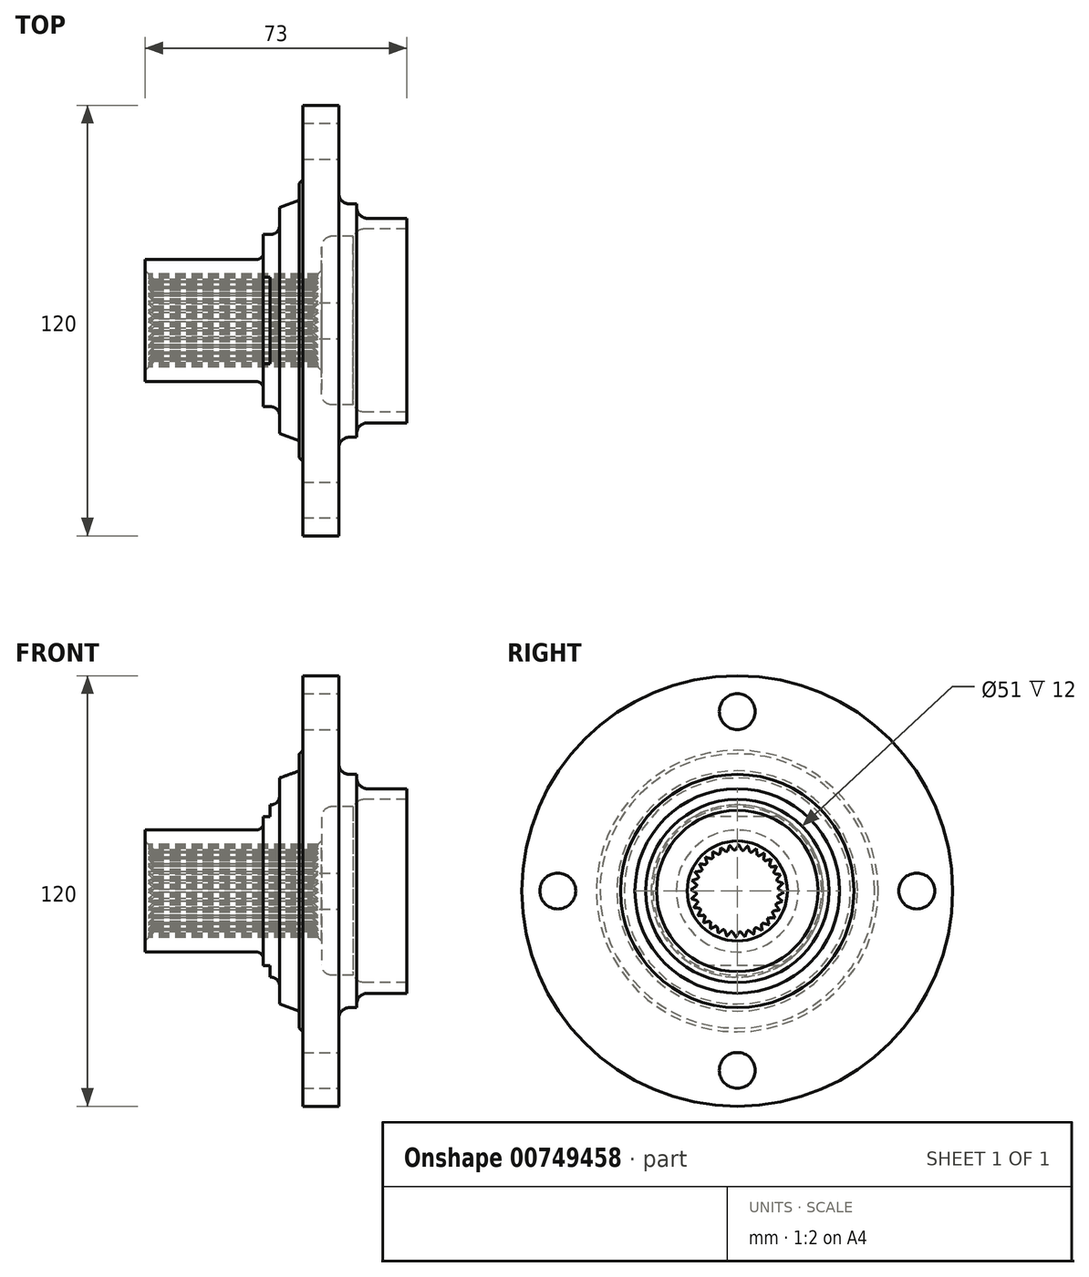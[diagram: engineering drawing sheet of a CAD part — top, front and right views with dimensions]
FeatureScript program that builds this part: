
annotation { "Feature Type Name" : "Feature", "Feature Type Description" : "" }
export const myFeature = defineFeature(function(context is Context, id is Id, definition is map)
    precondition{}
    {
        {
            var Q0;
            Q0=qCreatedBy(makeId("Front.planeOp"),FACE);
            var sketch = newSketch(context, id + "F0", { "sketchPlane" : qUnion([Q0])});
            skLineSegment(sketch, "E0", {"start": v(0, 0) * mm, "end": v(66.1, 0) * mm, "construction": true});
            skLineSegment(sketch, "E1", {"start": v(0, 17) * mm, "end": v(31, 17) * mm});
            skLineSegment(sketch, "E2", {"start": v(33, 19) * mm, "end": v(33, 24) * mm});
            skLineSegment(sketch, "E3", {"start": v(33, 24) * mm, "end": v(35, 24) * mm});
            skLineSegment(sketch, "E4", {"start": v(37.5, 26.5) * mm, "end": v(37.5, 31.5) * mm});
            skLineSegment(sketch, "E5", {"start": v(43, 33.5) * mm, "end": v(43, 38.25) * mm});
            skLineSegment(sketch, "E6", {"start": v(44, 39.25) * mm, "end": v(44, 60) * mm});
            skLineSegment(sketch, "E7", {"start": v(44, 60) * mm, "end": v(54, 60) * mm});
            skLineSegment(sketch, "E8", {"start": v(54, 60) * mm, "end": v(54, 35.5) * mm});
            skLineSegment(sketch, "E9", {"start": v(37.5, 31.5) * mm, "end": v(43, 33.5) * mm});
            skLineSegment(sketch, "E10", {"start": v(43, 38.25) * mm, "end": v(44, 39.25) * mm});
            skLineSegment(sketch, "E11", {"start": v(57, 32.5) * mm, "end": v(59, 32.5) * mm});
            skLineSegment(sketch, "E12", {"start": v(59, 32.5) * mm, "end": v(59, 31.5) * mm});
            skLineSegment(sketch, "E13", {"start": v(62, 28.5) * mm, "end": v(73, 28.5) * mm});
            skLineSegment(sketch, "E14", {"start": v(73, 28.5) * mm, "end": v(73, 25.5) * mm});
            skLineSegment(sketch, "E15", {"start": v(73, 25.5) * mm, "end": v(61, 25.5) * mm});
            skLineSegment(sketch, "E16", {"start": v(58, 23.5) * mm, "end": v(58, 22.5) * mm});
            skLineSegment(sketch, "E17", {"start": v(58, 23.5) * mm, "end": v(52.2, 23.5) * mm});
            skLineSegment(sketch, "E18", {"start": v(49.2, 20.5) * mm, "end": v(49.2, 11.45) * mm});
            skLineSegment(sketch, "E19", {"start": v(49.2, 11.45) * mm, "end": v(0, 11.45) * mm});
            skLineSegment(sketch, "E20", {"start": v(0, 11.45) * mm, "end": v(0, 17) * mm});
            skPoint(sketch, "E21.visualSharp", {"position": v(54, 32.5) * mm});
            skArc(sketch, "E21.filletArc", {"start": v(54, 35.5) * mm, "mid": v(54.88, 33.38) * mm, "end": v(57, 32.5) * mm});
            skPoint(sketch, "E22.visualSharp", {"position": v(59, 28.5) * mm});
            skArc(sketch, "E22.filletArc", {"start": v(59, 31.5) * mm, "mid": v(59.88, 29.38) * mm, "end": v(62, 28.5) * mm});
            skPoint(sketch, "E23.visualSharp", {"position": v(37.5, 24) * mm});
            skArc(sketch, "E23.filletArc", {"start": v(35, 24) * mm, "mid": v(36.77, 24.73) * mm, "end": v(37.5, 26.5) * mm});
            skPoint(sketch, "E24.visualSharp", {"position": v(33, 17) * mm});
            skArc(sketch, "E24.filletArc", {"start": v(31, 17) * mm, "mid": v(32.41, 17.59) * mm, "end": v(33, 19) * mm});
            skPoint(sketch, "E25.visualSharp", {"position": v(58, 25.5) * mm});
            skArc(sketch, "E25.filletArc", {"start": v(61, 25.5) * mm, "mid": v(58.88, 24.62) * mm, "end": v(58, 22.5) * mm});
            skPoint(sketch, "E26.visualSharp", {"position": v(49.2, 23.5) * mm});
            skArc(sketch, "E26.filletArc", {"start": v(52.2, 23.5) * mm, "mid": v(50.08, 22.62) * mm, "end": v(49.2, 20.5) * mm});
            skSolve(sketch);
        }
        {
            var Q0;
            Q0=makeQuery(id+"F0.imprint","IMPRINT",FACE,{"disambiguationData":[TD([[makeQuery(id+"F0.imprint","IMPRINT",EDGE,{"derivedFrom":sQuery(id+"F0.wireOp",EDGE,"E1")}),-1.0]])]});
            var Q1;
            Q1=sQuery(id+"F0.wireOp",EDGE,"E0");
            revolve(context, id + "F1", {"surfaceOperationType" : NewSurfaceOperationType.NEW, "entities" : qUnion([Q0]), "axis" : qUnion([Q1]), "revolveType" : RevolveType.FULL});
        }
        {
            var Q0;
            Q0=makeQuery(id+"F1.opRevolve","SWEPT_EDGE",EDGE,{"disambiguationData":[OSD([sQuery(id+"F0.wireOp",EDGE,"E19"),sQuery(id+"F0.wireOp",EDGE,"E20")])]});
            var Q1;
            Q1=makeQuery(id+"F1.opRevolve","SWEPT_EDGE",EDGE,{"disambiguationData":[OSD([sQuery(id+"F0.wireOp",EDGE,"E18"),sQuery(id+"F0.wireOp",EDGE,"E19")])]});
            chamfer(context, id + "F2", {"entities" : qUnion([Q0, Q1]), "width" : 2.5 * mm, "tangentPropagation" : true});
        }
        {
            var Q0;
            Q0=makeQuery(id+"F1.opRevolve","SWEPT_FACE",FACE,{"disambiguationData":[OSD([sQuery(id+"F0.wireOp",EDGE,"E2")])]});
            var sketch = newSketch(context, id + "F3", { "sketchPlane" : qUnion([Q0])});
            skLineSegment(sketch, "E27.bottom", {"start": v(-22.18, 27.37) * mm, "end": v(36.83, 27.37) * mm});
            skLineSegment(sketch, "E27.top", {"start": v(-22.18, 20.75) * mm, "end": v(36.83, 20.75) * mm});
            skLineSegment(sketch, "E27.left", {"start": v(-22.18, 27.37) * mm, "end": v(-22.18, 20.75) * mm});
            skLineSegment(sketch, "E27.right", {"start": v(36.83, 27.37) * mm, "end": v(36.83, 20.75) * mm});
            skLineSegment(sketch, "E28.MirrorCS", {"start": v(-22.18, -27.37) * mm, "end": v(36.83, -27.37) * mm});
            skLineSegment(sketch, "E29.MirrorCS", {"start": v(36.83, -27.37) * mm, "end": v(36.83, -20.75) * mm});
            skLineSegment(sketch, "E30.MirrorCS", {"start": v(-22.18, -20.75) * mm, "end": v(36.83, -20.75) * mm});
            skLineSegment(sketch, "E31.MirrorCS", {"start": v(-22.18, -27.37) * mm, "end": v(-22.18, -20.75) * mm});
            skSolve(sketch);
        }
        {
            var Q0;
            Q0 = qSketchRegion(id + "F3", true);
            extrude(context, id + "F4", {"entities" : qUnion([Q0]), "operationType" : NewBodyOperationType.REMOVE, "oppositeDirection" : true, "depth" : 1.8 * mm, "offsetDistance" : 25 * mm});
        }
        {
            var Q0;
            Q0=makeQuery(id+"F1.opRevolve","SWEPT_FACE",FACE,{"disambiguationData":[OSD([sQuery(id+"F0.wireOp",EDGE,"E20")])]});
            var sketch = newSketch(context, id + "F5", { "sketchPlane" : qUnion([Q0])});
            skCircle(sketch, "E32.0", {"center": v(0, 0) * mm, "radius": 11.45 * mm});
            skCircle(sketch, "E33.0", {"center": v(0, 0) * mm, "radius": 17 * mm});
            skLineSegment(sketch, "E34", {"start": v(-3.36, 7.8) * mm, "end": v(-0.4, 12.94) * mm});
            skLineSegment(sketch, "E35", {"start": v(-0.4, 12.94) * mm, "end": v(2.58, 7.8) * mm});
            skLineSegment(sketch, "E36", {"start": v(2.58, 7.8) * mm, "end": v(-3.36, 7.8) * mm});
            skLineSegment(sketch, "E37.1.0", {"start": v(-4.82, 7) * mm, "end": v(-2.9, 12.62) * mm});
            skLineSegment(sketch, "E37.1.1", {"start": v(-2.9, 12.62) * mm, "end": v(1, 8.15) * mm});
            skLineSegment(sketch, "E37.1.2", {"start": v(1, 8.15) * mm, "end": v(-4.82, 7) * mm});
            skLineSegment(sketch, "E37.2.0", {"start": v(-6.09, 5.92) * mm, "end": v(-5.31, 11.8) * mm});
            skLineSegment(sketch, "E37.2.1", {"start": v(-5.31, 11.8) * mm, "end": v(-0.6, 8.2) * mm});
            skLineSegment(sketch, "E37.2.2", {"start": v(-0.6, 8.2) * mm, "end": v(-6.09, 5.92) * mm});
            skLineSegment(sketch, "E37.3.0", {"start": v(-7.13, 4.62) * mm, "end": v(-7.52, 10.55) * mm});
            skLineSegment(sketch, "E37.3.1", {"start": v(-7.52, 10.55) * mm, "end": v(-2.19, 7.92) * mm});
            skLineSegment(sketch, "E37.3.2", {"start": v(-2.19, 7.92) * mm, "end": v(-7.13, 4.62) * mm});
            skLineSegment(sketch, "E37.4.0", {"start": v(-7.9, 3.14) * mm, "end": v(-9.43, 8.88) * mm});
            skLineSegment(sketch, "E37.4.1", {"start": v(-9.43, 8.88) * mm, "end": v(-3.7, 7.34) * mm});
            skLineSegment(sketch, "E37.4.2", {"start": v(-3.7, 7.34) * mm, "end": v(-7.9, 3.14) * mm});
            skLineSegment(sketch, "E37.5.0", {"start": v(-8.35, 1.54) * mm, "end": v(-10.98, 6.87) * mm});
            skLineSegment(sketch, "E37.5.1", {"start": v(-10.98, 6.87) * mm, "end": v(-5.05, 6.48) * mm});
            skLineSegment(sketch, "E37.5.2", {"start": v(-5.05, 6.48) * mm, "end": v(-8.35, 1.54) * mm});
            skLineSegment(sketch, "E37.6.0", {"start": v(-8.5, -0.12) * mm, "end": v(-12.1, 4.6) * mm});
            skLineSegment(sketch, "E37.6.1", {"start": v(-12.1, 4.6) * mm, "end": v(-6.22, 5.37) * mm});
            skLineSegment(sketch, "E37.6.2", {"start": v(-6.22, 5.37) * mm, "end": v(-8.5, -0.12) * mm});
            skLineSegment(sketch, "E37.7.0", {"start": v(-8.3, -1.77) * mm, "end": v(-12.77, 2.14) * mm});
            skLineSegment(sketch, "E37.7.1", {"start": v(-12.77, 2.14) * mm, "end": v(-7.15, 4.05) * mm});
            skLineSegment(sketch, "E37.7.2", {"start": v(-7.15, 4.05) * mm, "end": v(-8.3, -1.77) * mm});
            skLineSegment(sketch, "E37.8.0", {"start": v(-7.8, -3.36) * mm, "end": v(-12.94, -0.4) * mm});
            skLineSegment(sketch, "E37.8.1", {"start": v(-12.94, -0.4) * mm, "end": v(-7.8, 2.58) * mm});
            skLineSegment(sketch, "E37.8.2", {"start": v(-7.8, 2.58) * mm, "end": v(-7.8, -3.36) * mm});
            skLineSegment(sketch, "E37.9.0", {"start": v(-7, -4.82) * mm, "end": v(-12.62, -2.9) * mm});
            skLineSegment(sketch, "E37.9.1", {"start": v(-12.62, -2.9) * mm, "end": v(-8.15, 1) * mm});
            skLineSegment(sketch, "E37.9.2", {"start": v(-8.15, 1) * mm, "end": v(-7, -4.82) * mm});
            skLineSegment(sketch, "E37.10.0", {"start": v(-5.92, -6.09) * mm, "end": v(-11.8, -5.31) * mm});
            skLineSegment(sketch, "E37.10.1", {"start": v(-11.8, -5.31) * mm, "end": v(-8.2, -0.6) * mm});
            skLineSegment(sketch, "E37.10.2", {"start": v(-8.2, -0.6) * mm, "end": v(-5.92, -6.09) * mm});
            skLineSegment(sketch, "E37.11.0", {"start": v(-4.62, -7.13) * mm, "end": v(-10.55, -7.52) * mm});
            skLineSegment(sketch, "E37.11.1", {"start": v(-10.55, -7.52) * mm, "end": v(-7.92, -2.19) * mm});
            skLineSegment(sketch, "E37.11.2", {"start": v(-7.92, -2.19) * mm, "end": v(-4.62, -7.13) * mm});
            skLineSegment(sketch, "E37.12.0", {"start": v(-3.14, -7.9) * mm, "end": v(-8.88, -9.43) * mm});
            skLineSegment(sketch, "E37.12.1", {"start": v(-8.88, -9.43) * mm, "end": v(-7.34, -3.7) * mm});
            skLineSegment(sketch, "E37.12.2", {"start": v(-7.34, -3.7) * mm, "end": v(-3.14, -7.9) * mm});
            skLineSegment(sketch, "E37.13.0", {"start": v(-1.54, -8.35) * mm, "end": v(-6.87, -10.98) * mm});
            skLineSegment(sketch, "E37.13.1", {"start": v(-6.87, -10.98) * mm, "end": v(-6.48, -5.05) * mm});
            skLineSegment(sketch, "E37.13.2", {"start": v(-6.48, -5.05) * mm, "end": v(-1.54, -8.35) * mm});
            skLineSegment(sketch, "E37.14.0", {"start": v(0.12, -8.5) * mm, "end": v(-4.6, -12.1) * mm});
            skLineSegment(sketch, "E37.14.1", {"start": v(-4.6, -12.1) * mm, "end": v(-5.37, -6.22) * mm});
            skLineSegment(sketch, "E37.14.2", {"start": v(-5.37, -6.22) * mm, "end": v(0.12, -8.5) * mm});
            skLineSegment(sketch, "E37.15.0", {"start": v(1.77, -8.3) * mm, "end": v(-2.14, -12.77) * mm});
            skLineSegment(sketch, "E37.15.1", {"start": v(-2.14, -12.77) * mm, "end": v(-4.05, -7.15) * mm});
            skLineSegment(sketch, "E37.15.2", {"start": v(-4.05, -7.15) * mm, "end": v(1.77, -8.3) * mm});
            skLineSegment(sketch, "E37.16.0", {"start": v(3.36, -7.8) * mm, "end": v(0.4, -12.94) * mm});
            skLineSegment(sketch, "E37.16.1", {"start": v(0.4, -12.94) * mm, "end": v(-2.58, -7.8) * mm});
            skLineSegment(sketch, "E37.16.2", {"start": v(-2.58, -7.8) * mm, "end": v(3.36, -7.8) * mm});
            skLineSegment(sketch, "E37.17.0", {"start": v(4.82, -7) * mm, "end": v(2.9, -12.62) * mm});
            skLineSegment(sketch, "E37.17.1", {"start": v(2.9, -12.62) * mm, "end": v(-1, -8.15) * mm});
            skLineSegment(sketch, "E37.17.2", {"start": v(-1, -8.15) * mm, "end": v(4.82, -7) * mm});
            skLineSegment(sketch, "E37.18.0", {"start": v(6.09, -5.92) * mm, "end": v(5.31, -11.8) * mm});
            skLineSegment(sketch, "E37.18.1", {"start": v(5.31, -11.8) * mm, "end": v(0.6, -8.2) * mm});
            skLineSegment(sketch, "E37.18.2", {"start": v(0.6, -8.2) * mm, "end": v(6.09, -5.92) * mm});
            skLineSegment(sketch, "E37.19.0", {"start": v(7.13, -4.62) * mm, "end": v(7.52, -10.55) * mm});
            skLineSegment(sketch, "E37.19.1", {"start": v(7.52, -10.55) * mm, "end": v(2.19, -7.92) * mm});
            skLineSegment(sketch, "E37.19.2", {"start": v(2.19, -7.92) * mm, "end": v(7.13, -4.62) * mm});
            skLineSegment(sketch, "E37.20.0", {"start": v(7.9, -3.14) * mm, "end": v(9.43, -8.88) * mm});
            skLineSegment(sketch, "E37.20.1", {"start": v(9.43, -8.88) * mm, "end": v(3.7, -7.34) * mm});
            skLineSegment(sketch, "E37.20.2", {"start": v(3.7, -7.34) * mm, "end": v(7.9, -3.14) * mm});
            skLineSegment(sketch, "E37.21.0", {"start": v(8.35, -1.54) * mm, "end": v(10.98, -6.87) * mm});
            skLineSegment(sketch, "E37.21.1", {"start": v(10.98, -6.87) * mm, "end": v(5.05, -6.48) * mm});
            skLineSegment(sketch, "E37.21.2", {"start": v(5.05, -6.48) * mm, "end": v(8.35, -1.54) * mm});
            skLineSegment(sketch, "E37.22.0", {"start": v(8.5, 0.12) * mm, "end": v(12.1, -4.6) * mm});
            skLineSegment(sketch, "E37.22.1", {"start": v(12.1, -4.6) * mm, "end": v(6.22, -5.37) * mm});
            skLineSegment(sketch, "E37.22.2", {"start": v(6.22, -5.37) * mm, "end": v(8.5, 0.12) * mm});
            skLineSegment(sketch, "E37.23.0", {"start": v(8.3, 1.77) * mm, "end": v(12.77, -2.14) * mm});
            skLineSegment(sketch, "E37.23.1", {"start": v(12.77, -2.14) * mm, "end": v(7.15, -4.05) * mm});
            skLineSegment(sketch, "E37.23.2", {"start": v(7.15, -4.05) * mm, "end": v(8.3, 1.77) * mm});
            skLineSegment(sketch, "E37.24.0", {"start": v(7.8, 3.36) * mm, "end": v(12.94, 0.4) * mm});
            skLineSegment(sketch, "E37.24.1", {"start": v(12.94, 0.4) * mm, "end": v(7.8, -2.58) * mm});
            skLineSegment(sketch, "E37.24.2", {"start": v(7.8, -2.58) * mm, "end": v(7.8, 3.36) * mm});
            skLineSegment(sketch, "E37.25.0", {"start": v(7, 4.82) * mm, "end": v(12.62, 2.9) * mm});
            skLineSegment(sketch, "E37.25.1", {"start": v(12.62, 2.9) * mm, "end": v(8.15, -1) * mm});
            skLineSegment(sketch, "E37.25.2", {"start": v(8.15, -1) * mm, "end": v(7, 4.82) * mm});
            skLineSegment(sketch, "E37.26.0", {"start": v(5.92, 6.09) * mm, "end": v(11.8, 5.31) * mm});
            skLineSegment(sketch, "E37.26.1", {"start": v(11.8, 5.31) * mm, "end": v(8.2, 0.6) * mm});
            skLineSegment(sketch, "E37.26.2", {"start": v(8.2, 0.6) * mm, "end": v(5.92, 6.09) * mm});
            skLineSegment(sketch, "E37.27.0", {"start": v(4.62, 7.13) * mm, "end": v(10.55, 7.52) * mm});
            skLineSegment(sketch, "E37.27.1", {"start": v(10.55, 7.52) * mm, "end": v(7.92, 2.19) * mm});
            skLineSegment(sketch, "E37.27.2", {"start": v(7.92, 2.19) * mm, "end": v(4.62, 7.13) * mm});
            skLineSegment(sketch, "E37.28.0", {"start": v(3.14, 7.9) * mm, "end": v(8.88, 9.43) * mm});
            skLineSegment(sketch, "E37.28.1", {"start": v(8.88, 9.43) * mm, "end": v(7.34, 3.7) * mm});
            skLineSegment(sketch, "E37.28.2", {"start": v(7.34, 3.7) * mm, "end": v(3.14, 7.9) * mm});
            skLineSegment(sketch, "E37.29.0", {"start": v(1.54, 8.35) * mm, "end": v(6.87, 10.98) * mm});
            skLineSegment(sketch, "E37.29.1", {"start": v(6.87, 10.98) * mm, "end": v(6.48, 5.05) * mm});
            skLineSegment(sketch, "E37.29.2", {"start": v(6.48, 5.05) * mm, "end": v(1.54, 8.35) * mm});
            skLineSegment(sketch, "E37.30.0", {"start": v(-0.12, 8.5) * mm, "end": v(4.6, 12.1) * mm});
            skLineSegment(sketch, "E37.30.1", {"start": v(4.6, 12.1) * mm, "end": v(5.37, 6.22) * mm});
            skLineSegment(sketch, "E37.30.2", {"start": v(5.37, 6.22) * mm, "end": v(-0.12, 8.5) * mm});
            skLineSegment(sketch, "E37.31.0", {"start": v(-1.77, 8.3) * mm, "end": v(2.14, 12.77) * mm});
            skLineSegment(sketch, "E37.31.1", {"start": v(2.14, 12.77) * mm, "end": v(4.05, 7.15) * mm});
            skLineSegment(sketch, "E37.31.2", {"start": v(4.05, 7.15) * mm, "end": v(-1.77, 8.3) * mm});
            skSolve(sketch);
        }
        {
            var Q0;
            {var subQ0=sQuery(id+"F5.wireOp",EDGE,"E37.1.1");var subQ1=sQuery(id+"F5.wireOp",EDGE,"E32.0");var subQ2=makeQuery(id+"F5.imprint","INTERSECT",VERTEX,{"derivedFrom":[subQ1,subQ0]});Q0=makeQuery(id+"F5.imprint","IMPRINT",FACE,{"disambiguationData":[TD([[makeQuery(id+"F5.imprint","IMPRINT",EDGE,{"disambiguationData":[TD([[subQ2,-1.0]])],"derivedFrom":subQ1}),-1.0]])]});}
            var Q1;
            {var subQ0=sQuery(id+"F5.wireOp",EDGE,"E35");var subQ1=sQuery(id+"F5.wireOp",EDGE,"E32.0");var subQ2=makeQuery(id+"F5.imprint","INTERSECT",VERTEX,{"derivedFrom":[subQ1,subQ0]});Q1=makeQuery(id+"F5.imprint","IMPRINT",FACE,{"disambiguationData":[TD([[makeQuery(id+"F5.imprint","IMPRINT",EDGE,{"disambiguationData":[TD([[subQ2,-1.0]])],"derivedFrom":subQ1}),-1.0]])]});}
            var Q2;
            {var subQ0=sQuery(id+"F5.wireOp",EDGE,"E37.2.1");var subQ1=sQuery(id+"F5.wireOp",EDGE,"E32.0");var subQ2=makeQuery(id+"F5.imprint","INTERSECT",VERTEX,{"derivedFrom":[subQ1,subQ0]});Q2=makeQuery(id+"F5.imprint","IMPRINT",FACE,{"disambiguationData":[TD([[makeQuery(id+"F5.imprint","IMPRINT",EDGE,{"disambiguationData":[TD([[subQ2,-1.0]])],"derivedFrom":subQ1}),-1.0]])]});}
            var Q3;
            {var subQ0=sQuery(id+"F5.wireOp",EDGE,"E37.4.1");var subQ1=sQuery(id+"F5.wireOp",EDGE,"E32.0");var subQ2=makeQuery(id+"F5.imprint","INTERSECT",VERTEX,{"derivedFrom":[subQ1,subQ0]});Q3=makeQuery(id+"F5.imprint","IMPRINT",FACE,{"disambiguationData":[TD([[makeQuery(id+"F5.imprint","IMPRINT",EDGE,{"disambiguationData":[TD([[subQ2,-1.0]])],"derivedFrom":subQ1}),-1.0]])]});}
            var Q4;
            {var subQ0=sQuery(id+"F5.wireOp",EDGE,"E37.5.1");var subQ1=sQuery(id+"F5.wireOp",EDGE,"E32.0");var subQ2=makeQuery(id+"F5.imprint","INTERSECT",VERTEX,{"derivedFrom":[subQ1,subQ0]});Q4=makeQuery(id+"F5.imprint","IMPRINT",FACE,{"disambiguationData":[TD([[makeQuery(id+"F5.imprint","IMPRINT",EDGE,{"disambiguationData":[TD([[subQ2,-1.0]])],"derivedFrom":subQ1}),-1.0]])]});}
            var Q5;
            {var subQ0=sQuery(id+"F5.wireOp",EDGE,"E37.6.1");var subQ1=sQuery(id+"F5.wireOp",EDGE,"E32.0");var subQ2=makeQuery(id+"F5.imprint","INTERSECT",VERTEX,{"derivedFrom":[subQ1,subQ0]});Q5=makeQuery(id+"F5.imprint","IMPRINT",FACE,{"disambiguationData":[TD([[makeQuery(id+"F5.imprint","IMPRINT",EDGE,{"disambiguationData":[TD([[subQ2,-1.0]])],"derivedFrom":subQ1}),-1.0]])]});}
            var Q6;
            {var subQ0=sQuery(id+"F5.wireOp",EDGE,"E37.7.1");var subQ1=sQuery(id+"F5.wireOp",EDGE,"E32.0");var subQ2=makeQuery(id+"F5.imprint","INTERSECT",VERTEX,{"derivedFrom":[subQ1,subQ0]});Q6=makeQuery(id+"F5.imprint","IMPRINT",FACE,{"disambiguationData":[TD([[makeQuery(id+"F5.imprint","IMPRINT",EDGE,{"disambiguationData":[TD([[subQ2,-1.0]])],"derivedFrom":subQ1}),-1.0]])]});}
            var Q7;
            {var subQ0=sQuery(id+"F5.wireOp",EDGE,"E37.8.1");var subQ1=sQuery(id+"F5.wireOp",EDGE,"E32.0");var subQ2=makeQuery(id+"F5.imprint","INTERSECT",VERTEX,{"derivedFrom":[subQ1,subQ0]});Q7=makeQuery(id+"F5.imprint","IMPRINT",FACE,{"disambiguationData":[TD([[makeQuery(id+"F5.imprint","IMPRINT",EDGE,{"disambiguationData":[TD([[subQ2,-1.0]])],"derivedFrom":subQ1}),-1.0]])]});}
            var Q8;
            {var subQ0=sQuery(id+"F5.wireOp",EDGE,"E37.9.1");var subQ1=sQuery(id+"F5.wireOp",EDGE,"E32.0");var subQ2=makeQuery(id+"F5.imprint","INTERSECT",VERTEX,{"derivedFrom":[subQ1,subQ0]});Q8=makeQuery(id+"F5.imprint","IMPRINT",FACE,{"disambiguationData":[TD([[makeQuery(id+"F5.imprint","IMPRINT",EDGE,{"disambiguationData":[TD([[subQ2,-1.0]])],"derivedFrom":subQ1}),-1.0]])]});}
            var Q9;
            {var subQ0=sQuery(id+"F5.wireOp",EDGE,"E37.10.1");var subQ1=sQuery(id+"F5.wireOp",EDGE,"E32.0");var subQ2=makeQuery(id+"F5.imprint","INTERSECT",VERTEX,{"derivedFrom":[subQ1,subQ0]});Q9=makeQuery(id+"F5.imprint","IMPRINT",FACE,{"disambiguationData":[TD([[makeQuery(id+"F5.imprint","IMPRINT",EDGE,{"disambiguationData":[TD([[subQ2,-1.0]])],"derivedFrom":subQ1}),-1.0]])]});}
            var Q10;
            {var subQ0=sQuery(id+"F5.wireOp",EDGE,"E37.12.1");var subQ1=sQuery(id+"F5.wireOp",EDGE,"E32.0");var subQ2=makeQuery(id+"F5.imprint","INTERSECT",VERTEX,{"derivedFrom":[subQ1,subQ0]});Q10=makeQuery(id+"F5.imprint","IMPRINT",FACE,{"disambiguationData":[TD([[makeQuery(id+"F5.imprint","IMPRINT",EDGE,{"disambiguationData":[TD([[subQ2,-1.0]])],"derivedFrom":subQ1}),-1.0]])]});}
            var Q11;
            {var subQ0=sQuery(id+"F5.wireOp",EDGE,"E37.31.1");var subQ1=sQuery(id+"F5.wireOp",EDGE,"E32.0");var subQ2=makeQuery(id+"F5.imprint","INTERSECT",VERTEX,{"derivedFrom":[subQ1,subQ0]});Q11=makeQuery(id+"F5.imprint","IMPRINT",FACE,{"disambiguationData":[TD([[makeQuery(id+"F5.imprint","IMPRINT",EDGE,{"disambiguationData":[TD([[subQ2,-1.0]])],"derivedFrom":subQ1}),-1.0]])]});}
            var Q12;
            {var subQ0=sQuery(id+"F5.wireOp",EDGE,"E37.3.1");var subQ1=sQuery(id+"F5.wireOp",EDGE,"E32.0");var subQ2=makeQuery(id+"F5.imprint","INTERSECT",VERTEX,{"derivedFrom":[subQ1,subQ0]});Q12=makeQuery(id+"F5.imprint","IMPRINT",FACE,{"disambiguationData":[TD([[makeQuery(id+"F5.imprint","IMPRINT",EDGE,{"disambiguationData":[TD([[subQ2,-1.0]])],"derivedFrom":subQ1}),-1.0]])]});}
            var Q13;
            {var subQ0=sQuery(id+"F5.wireOp",EDGE,"E37.30.1");var subQ1=sQuery(id+"F5.wireOp",EDGE,"E32.0");var subQ2=makeQuery(id+"F5.imprint","INTERSECT",VERTEX,{"derivedFrom":[subQ1,subQ0]});Q13=makeQuery(id+"F5.imprint","IMPRINT",FACE,{"disambiguationData":[TD([[makeQuery(id+"F5.imprint","IMPRINT",EDGE,{"disambiguationData":[TD([[subQ2,-1.0]])],"derivedFrom":subQ1}),-1.0]])]});}
            var Q14;
            {var subQ0=sQuery(id+"F5.wireOp",EDGE,"E37.29.1");var subQ1=sQuery(id+"F5.wireOp",EDGE,"E32.0");var subQ2=makeQuery(id+"F5.imprint","INTERSECT",VERTEX,{"derivedFrom":[subQ1,subQ0]});Q14=makeQuery(id+"F5.imprint","IMPRINT",FACE,{"disambiguationData":[TD([[makeQuery(id+"F5.imprint","IMPRINT",EDGE,{"disambiguationData":[TD([[subQ2,-1.0]])],"derivedFrom":subQ1}),-1.0]])]});}
            var Q15;
            {var subQ0=sQuery(id+"F5.wireOp",EDGE,"E37.28.1");var subQ1=sQuery(id+"F5.wireOp",EDGE,"E32.0");var subQ2=makeQuery(id+"F5.imprint","INTERSECT",VERTEX,{"derivedFrom":[subQ1,subQ0]});Q15=makeQuery(id+"F5.imprint","IMPRINT",FACE,{"disambiguationData":[TD([[makeQuery(id+"F5.imprint","IMPRINT",EDGE,{"disambiguationData":[TD([[subQ2,-1.0]])],"derivedFrom":subQ1}),-1.0]])]});}
            var Q16;
            {var subQ0=sQuery(id+"F5.wireOp",EDGE,"E37.27.1");var subQ1=sQuery(id+"F5.wireOp",EDGE,"E32.0");var subQ2=makeQuery(id+"F5.imprint","INTERSECT",VERTEX,{"derivedFrom":[subQ1,subQ0]});Q16=makeQuery(id+"F5.imprint","IMPRINT",FACE,{"disambiguationData":[TD([[makeQuery(id+"F5.imprint","IMPRINT",EDGE,{"disambiguationData":[TD([[subQ2,-1.0]])],"derivedFrom":subQ1}),-1.0]])]});}
            var Q17;
            {var subQ0=sQuery(id+"F5.wireOp",EDGE,"E37.26.1");var subQ1=sQuery(id+"F5.wireOp",EDGE,"E32.0");var subQ2=makeQuery(id+"F5.imprint","INTERSECT",VERTEX,{"derivedFrom":[subQ1,subQ0]});Q17=makeQuery(id+"F5.imprint","IMPRINT",FACE,{"disambiguationData":[TD([[makeQuery(id+"F5.imprint","IMPRINT",EDGE,{"disambiguationData":[TD([[subQ2,-1.0]])],"derivedFrom":subQ1}),-1.0]])]});}
            var Q18;
            {var subQ0=sQuery(id+"F5.wireOp",EDGE,"E37.25.1");var subQ1=sQuery(id+"F5.wireOp",EDGE,"E32.0");var subQ2=makeQuery(id+"F5.imprint","INTERSECT",VERTEX,{"derivedFrom":[subQ1,subQ0]});Q18=makeQuery(id+"F5.imprint","IMPRINT",FACE,{"disambiguationData":[TD([[makeQuery(id+"F5.imprint","IMPRINT",EDGE,{"disambiguationData":[TD([[subQ2,-1.0]])],"derivedFrom":subQ1}),-1.0]])]});}
            var Q19;
            {var subQ0=sQuery(id+"F5.wireOp",EDGE,"E37.24.0");var subQ1=sQuery(id+"F5.wireOp",EDGE,"E32.0");var subQ2=makeQuery(id+"F5.imprint","INTERSECT",VERTEX,{"derivedFrom":[subQ1,subQ0]});Q19=makeQuery(id+"F5.imprint","IMPRINT",FACE,{"disambiguationData":[TD([[makeQuery(id+"F5.imprint","IMPRINT",EDGE,{"disambiguationData":[TD([[subQ2,1.0]])],"derivedFrom":subQ1}),-1.0]])]});}
            var Q20;
            {var subQ0=sQuery(id+"F5.wireOp",EDGE,"E37.23.1");var subQ1=sQuery(id+"F5.wireOp",EDGE,"E32.0");var subQ2=makeQuery(id+"F5.imprint","INTERSECT",VERTEX,{"derivedFrom":[subQ1,subQ0]});Q20=makeQuery(id+"F5.imprint","IMPRINT",FACE,{"disambiguationData":[TD([[makeQuery(id+"F5.imprint","IMPRINT",EDGE,{"disambiguationData":[TD([[subQ2,-1.0]])],"derivedFrom":subQ1}),-1.0]])]});}
            var Q21;
            {var subQ0=sQuery(id+"F5.wireOp",EDGE,"E37.22.1");var subQ1=sQuery(id+"F5.wireOp",EDGE,"E32.0");var subQ2=makeQuery(id+"F5.imprint","INTERSECT",VERTEX,{"derivedFrom":[subQ1,subQ0]});Q21=makeQuery(id+"F5.imprint","IMPRINT",FACE,{"disambiguationData":[TD([[makeQuery(id+"F5.imprint","IMPRINT",EDGE,{"disambiguationData":[TD([[subQ2,-1.0]])],"derivedFrom":subQ1}),-1.0]])]});}
            var Q22;
            {var subQ0=sQuery(id+"F5.wireOp",EDGE,"E37.11.1");var subQ1=sQuery(id+"F5.wireOp",EDGE,"E32.0");var subQ2=makeQuery(id+"F5.imprint","INTERSECT",VERTEX,{"derivedFrom":[subQ1,subQ0]});Q22=makeQuery(id+"F5.imprint","IMPRINT",FACE,{"disambiguationData":[TD([[makeQuery(id+"F5.imprint","IMPRINT",EDGE,{"disambiguationData":[TD([[subQ2,-1.0]])],"derivedFrom":subQ1}),-1.0]])]});}
            var Q23;
            {var subQ0=sQuery(id+"F5.wireOp",EDGE,"E37.13.1");var subQ1=sQuery(id+"F5.wireOp",EDGE,"E32.0");var subQ2=makeQuery(id+"F5.imprint","INTERSECT",VERTEX,{"derivedFrom":[subQ1,subQ0]});Q23=makeQuery(id+"F5.imprint","IMPRINT",FACE,{"disambiguationData":[TD([[makeQuery(id+"F5.imprint","IMPRINT",EDGE,{"disambiguationData":[TD([[subQ2,-1.0]])],"derivedFrom":subQ1}),-1.0]])]});}
            var Q24;
            {var subQ0=sQuery(id+"F5.wireOp",EDGE,"E37.14.1");var subQ1=sQuery(id+"F5.wireOp",EDGE,"E32.0");var subQ2=makeQuery(id+"F5.imprint","INTERSECT",VERTEX,{"derivedFrom":[subQ1,subQ0]});Q24=makeQuery(id+"F5.imprint","IMPRINT",FACE,{"disambiguationData":[TD([[makeQuery(id+"F5.imprint","IMPRINT",EDGE,{"disambiguationData":[TD([[subQ2,-1.0]])],"derivedFrom":subQ1}),-1.0]])]});}
            var Q25;
            {var subQ0=sQuery(id+"F5.wireOp",EDGE,"E37.17.1");var subQ1=sQuery(id+"F5.wireOp",EDGE,"E32.0");var subQ2=makeQuery(id+"F5.imprint","INTERSECT",VERTEX,{"derivedFrom":[subQ1,subQ0]});Q25=makeQuery(id+"F5.imprint","IMPRINT",FACE,{"disambiguationData":[TD([[makeQuery(id+"F5.imprint","IMPRINT",EDGE,{"disambiguationData":[TD([[subQ2,-1.0]])],"derivedFrom":subQ1}),-1.0]])]});}
            var Q26;
            {var subQ0=sQuery(id+"F5.wireOp",EDGE,"E37.15.1");var subQ1=sQuery(id+"F5.wireOp",EDGE,"E32.0");var subQ2=makeQuery(id+"F5.imprint","INTERSECT",VERTEX,{"derivedFrom":[subQ1,subQ0]});Q26=makeQuery(id+"F5.imprint","IMPRINT",FACE,{"disambiguationData":[TD([[makeQuery(id+"F5.imprint","IMPRINT",EDGE,{"disambiguationData":[TD([[subQ2,-1.0]])],"derivedFrom":subQ1}),-1.0]])]});}
            var Q27;
            {var subQ0=sQuery(id+"F5.wireOp",EDGE,"E37.16.1");var subQ1=sQuery(id+"F5.wireOp",EDGE,"E32.0");var subQ2=makeQuery(id+"F5.imprint","INTERSECT",VERTEX,{"derivedFrom":[subQ1,subQ0]});Q27=makeQuery(id+"F5.imprint","IMPRINT",FACE,{"disambiguationData":[TD([[makeQuery(id+"F5.imprint","IMPRINT",EDGE,{"disambiguationData":[TD([[subQ2,-1.0]])],"derivedFrom":subQ1}),-1.0]])]});}
            var Q28;
            {var subQ0=sQuery(id+"F5.wireOp",EDGE,"E37.18.1");var subQ1=sQuery(id+"F5.wireOp",EDGE,"E32.0");var subQ2=makeQuery(id+"F5.imprint","INTERSECT",VERTEX,{"derivedFrom":[subQ1,subQ0]});Q28=makeQuery(id+"F5.imprint","IMPRINT",FACE,{"disambiguationData":[TD([[makeQuery(id+"F5.imprint","IMPRINT",EDGE,{"disambiguationData":[TD([[subQ2,-1.0]])],"derivedFrom":subQ1}),-1.0]])]});}
            var Q29;
            {var subQ0=sQuery(id+"F5.wireOp",EDGE,"E37.19.1");var subQ1=sQuery(id+"F5.wireOp",EDGE,"E32.0");var subQ2=makeQuery(id+"F5.imprint","INTERSECT",VERTEX,{"derivedFrom":[subQ1,subQ0]});Q29=makeQuery(id+"F5.imprint","IMPRINT",FACE,{"disambiguationData":[TD([[makeQuery(id+"F5.imprint","IMPRINT",EDGE,{"disambiguationData":[TD([[subQ2,-1.0]])],"derivedFrom":subQ1}),-1.0]])]});}
            var Q30;
            {var subQ0=sQuery(id+"F5.wireOp",EDGE,"E37.20.1");var subQ1=sQuery(id+"F5.wireOp",EDGE,"E32.0");var subQ2=makeQuery(id+"F5.imprint","INTERSECT",VERTEX,{"derivedFrom":[subQ1,subQ0]});Q30=makeQuery(id+"F5.imprint","IMPRINT",FACE,{"disambiguationData":[TD([[makeQuery(id+"F5.imprint","IMPRINT",EDGE,{"disambiguationData":[TD([[subQ2,-1.0]])],"derivedFrom":subQ1}),-1.0]])]});}
            var Q31;
            {var subQ0=sQuery(id+"F5.wireOp",EDGE,"E37.21.1");var subQ1=sQuery(id+"F5.wireOp",EDGE,"E32.0");var subQ2=makeQuery(id+"F5.imprint","INTERSECT",VERTEX,{"derivedFrom":[subQ1,subQ0]});Q31=makeQuery(id+"F5.imprint","IMPRINT",FACE,{"disambiguationData":[TD([[makeQuery(id+"F5.imprint","IMPRINT",EDGE,{"disambiguationData":[TD([[subQ2,-1.0]])],"derivedFrom":subQ1}),-1.0]])]});}
            extrude(context, id + "F6", {"entities" : qUnion([Q0, Q1, Q2, Q3, Q4, Q5, Q6, Q7, Q8, Q9, Q10, Q11, Q12, Q13, Q14, Q15, Q16, Q17, Q18, Q19, Q20, Q21, Q22, Q23, Q24, Q25, Q26, Q27, Q28, Q29, Q30, Q31]), "operationType" : NewBodyOperationType.REMOVE, "endBound" : BoundingType.THROUGH_ALL, "oppositeDirection" : true, "depth" : 25 * mm, "offsetDistance" : 25 * mm});
        }
        {
            var Q0;
            Q0=makeQuery(id+"F1.opRevolve","SWEPT_FACE",FACE,{"disambiguationData":[OSD([sQuery(id+"F0.wireOp",EDGE,"E8")])]});
            var sketch = newSketch(context, id + "F7", { "sketchPlane" : qUnion([Q0])});
            skCircle(sketch, "E38", {"center": v(0, 50) * mm, "radius": 5 * mm});
            skCircle(sketch, "E39.1.0", {"center": v(-50, 0) * mm, "radius": 5 * mm});
            skCircle(sketch, "E39.2.0", {"center": v(0, -50) * mm, "radius": 5 * mm});
            skPoint(sketch, "E39.center", {"position": v(0, 0) * mm});
            skCircle(sketch, "E40.1.3.0", {"center": v(50, 0) * mm, "radius": 5 * mm});
            skSolve(sketch);
        }
        {
            var Q0;
            Q0 = qSketchRegion(id + "F7", true);
            extrude(context, id + "F8", {"entities" : qUnion([Q0]), "operationType" : NewBodyOperationType.REMOVE, "oppositeDirection" : true, "depth" : 25 * mm, "offsetDistance" : 25 * mm});
        }
    });
